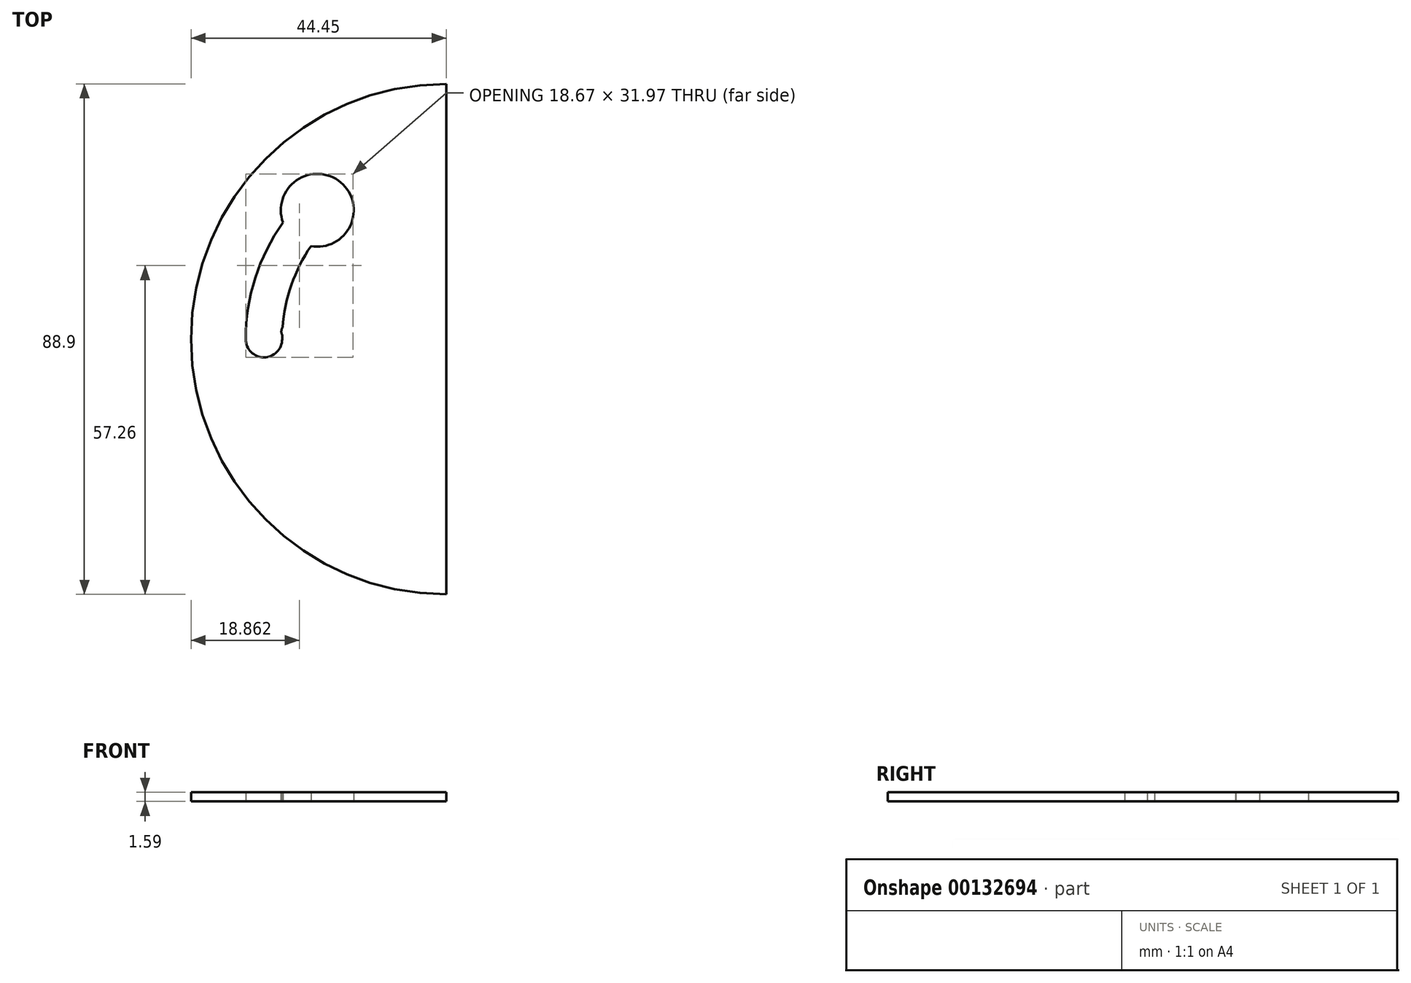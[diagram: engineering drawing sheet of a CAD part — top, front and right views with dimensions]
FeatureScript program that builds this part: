
annotation { "Feature Type Name" : "Feature", "Feature Type Description" : "" }
export const myFeature = defineFeature(function(context is Context, id is Id, definition is map)
    precondition{}
    {
        {
            var Q0;
            Q0=qCreatedBy(makeId("Top.planeOp"),FACE);
            var sketch = newSketch(context, id + "F0", { "sketchPlane" : qUnion([Q0])});
            skCircle(sketch, "E0", {"center": v(0, 0) * mm, "radius": 44.45 * mm});
            skLineSegment(sketch, "E1", {"start": v(0, 72.68) * mm, "end": v(0, -70.78) * mm});
            skLineSegment(sketch, "E2", {"start": v(70.46, 0) * mm, "end": v(34.93, 0) * mm});
            skArc(sketch, "E3", {"start": v(-34.92, 0) * mm, "mid": v(-31.75, -3.18) * mm, "end": v(-28.57, 0) * mm});
            skLineSegment(sketch, "E4.trimOffspring", {"start": v(-34.92, 0) * mm, "end": v(-64.18, 0) * mm});
            skArc(sketch, "E5.MirrorC", {"start": v(28.57, 0) * mm, "mid": v(31.75, 3.17) * mm, "end": v(34.92, 0) * mm});
            skArc(sketch, "E6", {"start": v(-23.54, 16.2) * mm, "mid": v(-26.97, 9.44) * mm, "end": v(-28.5, 2.01) * mm});
            skArc(sketch, "E7", {"start": v(-28.42, 20.3) * mm, "mid": v(-33.26, 10.66) * mm, "end": v(-34.92, 0) * mm});
            skArc(sketch, "E8.MirrorC", {"start": v(-23.54, 16.2) * mm, "mid": v(-18.37, 27.31) * mm, "end": v(-28.42, 20.3) * mm});
            skArc(sketch, "E9.MirrorC", {"start": v(23.54, -16.2) * mm, "mid": v(18.37, -27.31) * mm, "end": v(28.42, -20.3) * mm});
            skArc(sketch, "E10.trimOffspring", {"start": v(28.42, -20.3) * mm, "mid": v(33.26, -10.66) * mm, "end": v(34.92, 0) * mm});
            skArc(sketch, "E11.trimOffspring", {"start": v(23.54, -16.2) * mm, "mid": v(26.97, -9.44) * mm, "end": v(28.5, -2.01) * mm});
            skArc(sketch, "E12", {"start": v(-28.5, 2.01) * mm, "mid": v(-28.7, 1.38) * mm, "end": v(-28.57, 0.73) * mm});
            skArc(sketch, "E13.MirrorC", {"start": v(28.5, -2.01) * mm, "mid": v(28.7, -1.38) * mm, "end": v(28.57, -0.73) * mm});
            skArc(sketch, "E14.trimOffspring", {"start": v(-28.57, 0.73) * mm, "mid": v(-28.57, 0.36) * mm, "end": v(-28.58, 0) * mm});
            skArc(sketch, "E15.trimOffspring", {"start": v(28.57, -0.73) * mm, "mid": v(28.57, -0.36) * mm, "end": v(28.57, 0) * mm});
            skSolve(sketch);
        }
        {
            var Q0;
            Q0=makeQuery(id+"F0.imprint","IMPRINT",FACE,{"disambiguationData":[TD([[makeQuery(id+"F0.imprint","IMPRINT",EDGE,{"derivedFrom":sQuery(id+"F0.wireOp",EDGE,"E6")}),1.0]])]});
            var Q1;
            {var subQ1=sQuery(id+"F0.wireOp",EDGE,"E3");Q1=makeQuery(id+"F0.imprint","IMPRINT",FACE,{"disambiguationData":[TD([[makeQuery(id+"F0.imprint","IMPRINT",EDGE,{"derivedFrom":subQ1}),-1.0]])]});}
            extrude(context, id + "F1", {"entities" : qUnion([Q0, Q1]), "depth" : 1.59 * mm});
        }
    });
